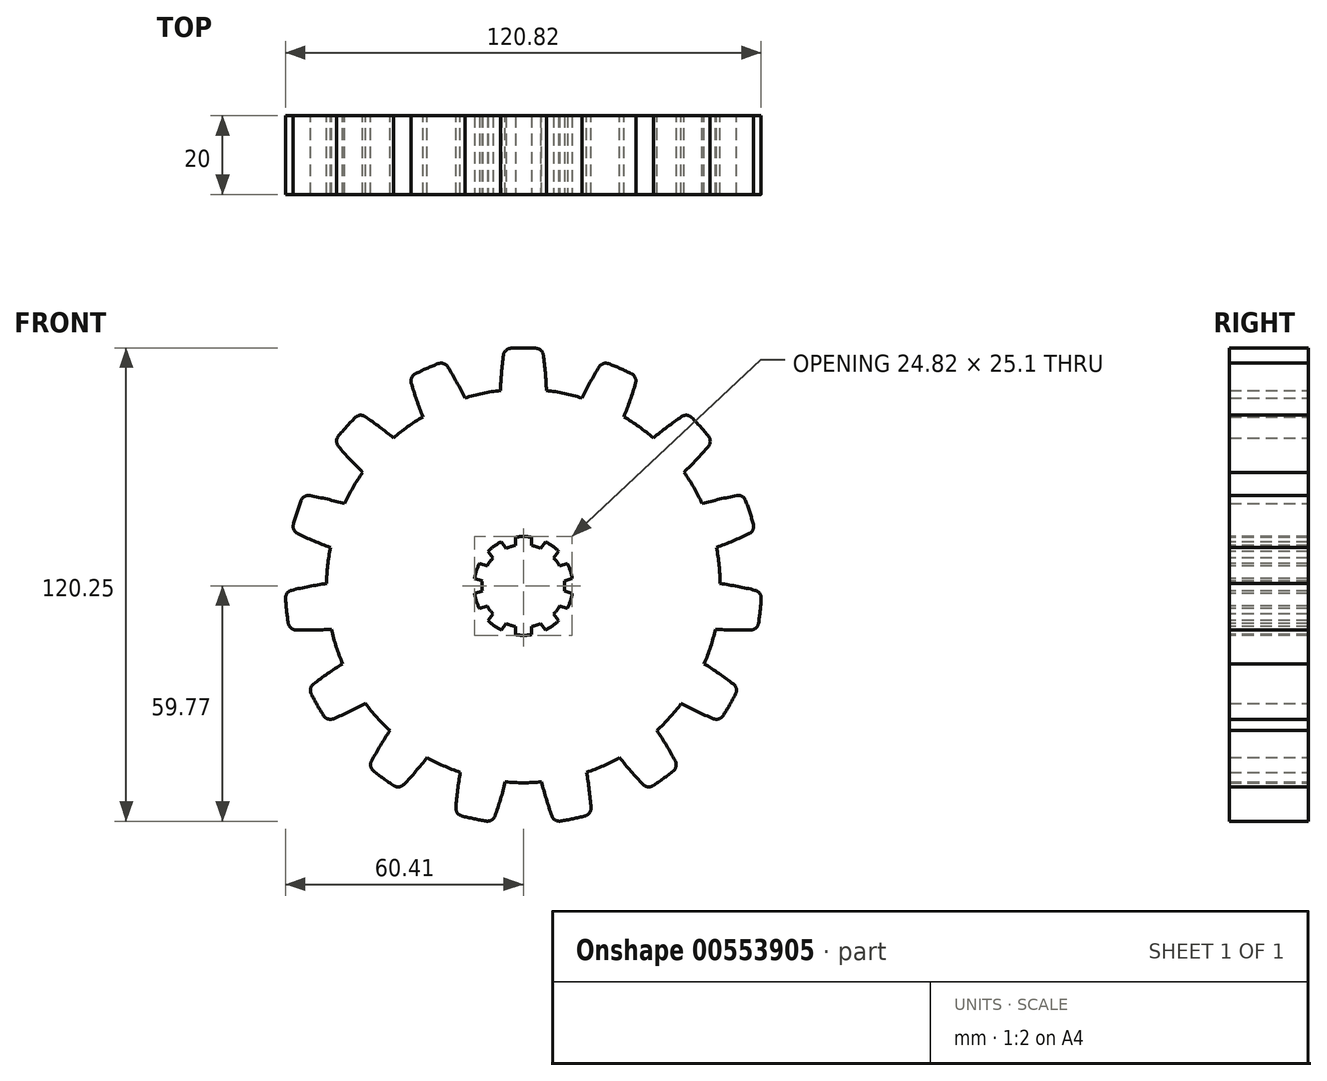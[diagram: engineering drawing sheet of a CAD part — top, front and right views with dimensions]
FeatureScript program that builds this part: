
annotation { "Feature Type Name" : "Feature", "Feature Type Description" : "" }
export const myFeature = defineFeature(function(context is Context, id is Id, definition is map)
    precondition{}
    {
        {
            var Q0;
            Q0=qCreatedBy(makeId("Front.planeOp"),FACE);
            var sketch = newSketch(context, id + "F0", { "sketchPlane" : qUnion([Q0])});
            skCircle(sketch, "E0", {"center": v(0, 0) * mm, "radius": 50 * mm});
            skLineSegment(sketch, "E1", {"start": v(-48.98, 46.5) * mm, "end": v(18.38, 46.5) * mm, "construction": true});
            skLineSegment(sketch, "E2", {"start": v(84.1, 97.1) * mm, "end": v(84.1, -36.75) * mm, "construction": true});
            skArc(sketch, "E3", {"start": v(-4.84, 60.29) * mm, "mid": v(-5.5, 54.99) * mm, "end": v(-5.84, 49.66) * mm});
            skArc(sketch, "E4.MirrorCS", {"start": v(4.84, 60.29) * mm, "mid": v(5.5, 54.99) * mm, "end": v(5.84, 49.66) * mm});
            skArc(sketch, "E5.trimOffspring", {"start": v(4.84, 60.29) * mm, "mid": v(0, 60.48) * mm, "end": v(-4.84, 60.29) * mm});
            skArc(sketch, "E6.1.0", {"start": v(-28.94, 53.11) * mm, "mid": v(-27.39, 48) * mm, "end": v(-25.54, 42.99) * mm});
            skArc(sketch, "E6.1.1", {"start": v(-20.1, 57.05) * mm, "mid": v(-24.6, 55.25) * mm, "end": v(-28.94, 53.11) * mm});
            skArc(sketch, "E6.1.2", {"start": v(-20.1, 57.05) * mm, "mid": v(-17.34, 52.47) * mm, "end": v(-14.86, 47.74) * mm});
            skArc(sketch, "E6.2.0", {"start": v(-48.04, 36.75) * mm, "mid": v(-44.54, 32.7) * mm, "end": v(-40.81, 28.88) * mm});
            skArc(sketch, "E6.2.1", {"start": v(-41.57, 43.94) * mm, "mid": v(-44.95, 40.47) * mm, "end": v(-48.04, 36.75) * mm});
            skArc(sketch, "E6.2.2", {"start": v(-41.57, 43.94) * mm, "mid": v(-37.19, 40.88) * mm, "end": v(-33, 37.57) * mm});
            skArc(sketch, "E6.3.0", {"start": v(-58.83, 14.03) * mm, "mid": v(-54, 11.76) * mm, "end": v(-49.03, 9.79) * mm});
            skArc(sketch, "E6.3.1", {"start": v(-55.84, 23.23) * mm, "mid": v(-57.52, 18.7) * mm, "end": v(-58.83, 14.03) * mm});
            skArc(sketch, "E6.3.2", {"start": v(-55.84, 23.23) * mm, "mid": v(-50.6, 22.22) * mm, "end": v(-45.42, 20.9) * mm});
            skArc(sketch, "E6.4.0", {"start": v(-59.45, -11.11) * mm, "mid": v(-54.11, -11.22) * mm, "end": v(-48.77, -11) * mm});
            skArc(sketch, "E6.4.1", {"start": v(-60.47, -1.5) * mm, "mid": v(-60.15, -6.32) * mm, "end": v(-59.45, -11.11) * mm});
            skArc(sketch, "E6.4.2", {"start": v(-60.47, -1.5) * mm, "mid": v(-55.26, -0.28) * mm, "end": v(-50, 0.62) * mm});
            skArc(sketch, "E6.5.0", {"start": v(-49.8, -34.33) * mm, "mid": v(-44.87, -32.26) * mm, "end": v(-40.08, -29.9) * mm});
            skArc(sketch, "E6.5.1", {"start": v(-54.63, -25.96) * mm, "mid": v(-52.38, -30.24) * mm, "end": v(-49.8, -34.33) * mm});
            skArc(sketch, "E6.5.2", {"start": v(-54.63, -25.96) * mm, "mid": v(-50.37, -22.73) * mm, "end": v(-45.93, -19.77) * mm});
            skArc(sketch, "E6.6.0", {"start": v(-31.52, -51.62) * mm, "mid": v(-27.87, -47.72) * mm, "end": v(-24.46, -43.6) * mm});
            skArc(sketch, "E6.6.1", {"start": v(-39.35, -45.93) * mm, "mid": v(-35.55, -48.93) * mm, "end": v(-31.52, -51.62) * mm});
            skArc(sketch, "E6.6.2", {"start": v(-39.35, -45.93) * mm, "mid": v(-36.77, -41.25) * mm, "end": v(-33.92, -36.74) * mm});
            skArc(sketch, "E6.7.0", {"start": v(-7.8, -59.98) * mm, "mid": v(-6.05, -54.93) * mm, "end": v(-4.6, -49.79) * mm});
            skArc(sketch, "E6.7.1", {"start": v(-17.27, -57.97) * mm, "mid": v(-12.58, -59.16) * mm, "end": v(-7.8, -59.98) * mm});
            skArc(sketch, "E6.7.2", {"start": v(-17.27, -57.97) * mm, "mid": v(-16.81, -52.64) * mm, "end": v(-16.04, -47.36) * mm});
            skArc(sketch, "E6.8.0", {"start": v(17.27, -57.97) * mm, "mid": v(16.81, -52.64) * mm, "end": v(16.04, -47.36) * mm});
            skArc(sketch, "E6.8.1", {"start": v(7.8, -59.98) * mm, "mid": v(12.58, -59.16) * mm, "end": v(17.27, -57.97) * mm});
            skArc(sketch, "E6.8.2", {"start": v(7.8, -59.98) * mm, "mid": v(6.05, -54.93) * mm, "end": v(4.6, -49.79) * mm});
            skArc(sketch, "E6.9.0", {"start": v(39.35, -45.93) * mm, "mid": v(36.77, -41.25) * mm, "end": v(33.92, -36.74) * mm});
            skArc(sketch, "E6.9.1", {"start": v(31.52, -51.62) * mm, "mid": v(35.55, -48.93) * mm, "end": v(39.35, -45.93) * mm});
            skArc(sketch, "E6.9.2", {"start": v(31.52, -51.62) * mm, "mid": v(27.87, -47.72) * mm, "end": v(24.46, -43.6) * mm});
            skArc(sketch, "E6.10.0", {"start": v(54.63, -25.96) * mm, "mid": v(50.37, -22.73) * mm, "end": v(45.93, -19.77) * mm});
            skArc(sketch, "E6.10.1", {"start": v(49.8, -34.33) * mm, "mid": v(52.38, -30.24) * mm, "end": v(54.63, -25.96) * mm});
            skArc(sketch, "E6.10.2", {"start": v(49.8, -34.33) * mm, "mid": v(44.87, -32.26) * mm, "end": v(40.08, -29.9) * mm});
            skArc(sketch, "E6.11.0", {"start": v(60.47, -1.5) * mm, "mid": v(55.26, -0.28) * mm, "end": v(50, 0.62) * mm});
            skArc(sketch, "E6.11.1", {"start": v(59.45, -11.11) * mm, "mid": v(60.15, -6.32) * mm, "end": v(60.47, -1.5) * mm});
            skArc(sketch, "E6.11.2", {"start": v(59.45, -11.11) * mm, "mid": v(54.11, -11.22) * mm, "end": v(48.77, -11) * mm});
            skArc(sketch, "E6.12.0", {"start": v(55.84, 23.23) * mm, "mid": v(50.6, 22.22) * mm, "end": v(45.42, 20.9) * mm});
            skArc(sketch, "E6.12.1", {"start": v(58.83, 14.03) * mm, "mid": v(57.52, 18.7) * mm, "end": v(55.84, 23.23) * mm});
            skArc(sketch, "E6.12.2", {"start": v(58.83, 14.03) * mm, "mid": v(54, 11.76) * mm, "end": v(49.03, 9.79) * mm});
            skArc(sketch, "E6.13.0", {"start": v(41.57, 43.94) * mm, "mid": v(37.19, 40.88) * mm, "end": v(33, 37.57) * mm});
            skArc(sketch, "E6.13.1", {"start": v(48.04, 36.75) * mm, "mid": v(44.95, 40.47) * mm, "end": v(41.57, 43.94) * mm});
            skArc(sketch, "E6.13.2", {"start": v(48.04, 36.75) * mm, "mid": v(44.54, 32.7) * mm, "end": v(40.81, 28.88) * mm});
            skArc(sketch, "E6.14.0", {"start": v(20.1, 57.05) * mm, "mid": v(17.34, 52.47) * mm, "end": v(14.86, 47.74) * mm});
            skArc(sketch, "E6.14.1", {"start": v(28.94, 53.11) * mm, "mid": v(24.6, 55.25) * mm, "end": v(20.1, 57.05) * mm});
            skArc(sketch, "E6.14.2", {"start": v(28.94, 53.11) * mm, "mid": v(27.39, 48) * mm, "end": v(25.54, 42.99) * mm});
            skSolve(sketch);
        }
        {
            var Q0;
            {var subQ0=sQuery(id+"F0.wireOp",EDGE,"E0");var subQ18=makeQuery(id+"F0.imprint","INTERSECT",VERTEX,{"derivedFrom":[subQ0,sQuery(id+"F0.wireOp",EDGE,"E6.11.0")]});Q0=makeQuery(id+"F0.imprint","IMPRINT",FACE,{"disambiguationData":[TD([[makeQuery(id+"F0.imprint","IMPRINT",EDGE,{"disambiguationData":[TD([[subQ18,-1.0]])],"derivedFrom":subQ0}),1.0]])]});}
            var Q1;
            {var subQ0=sQuery(id+"F0.wireOp",EDGE,"E6.1.0");Q1=makeQuery(id+"F0.imprint","IMPRINT",FACE,{"disambiguationData":[TD([[makeQuery(id+"F0.imprint","IMPRINT",EDGE,{"derivedFrom":subQ0}),1.0]])]});}
            var Q2;
            {var subQ0=sQuery(id+"F0.wireOp",EDGE,"E3");Q2=makeQuery(id+"F0.imprint","IMPRINT",FACE,{"disambiguationData":[TD([[makeQuery(id+"F0.imprint","IMPRINT",EDGE,{"derivedFrom":subQ0}),1.0]])]});}
            var Q3;
            {var subQ0=sQuery(id+"F0.wireOp",EDGE,"E6.14.0");Q3=makeQuery(id+"F0.imprint","IMPRINT",FACE,{"disambiguationData":[TD([[makeQuery(id+"F0.imprint","IMPRINT",EDGE,{"derivedFrom":subQ0}),1.0]])]});}
            var Q4;
            {var subQ0=sQuery(id+"F0.wireOp",EDGE,"E6.13.0");Q4=makeQuery(id+"F0.imprint","IMPRINT",FACE,{"disambiguationData":[TD([[makeQuery(id+"F0.imprint","IMPRINT",EDGE,{"derivedFrom":subQ0}),1.0]])]});}
            var Q5;
            {var subQ0=sQuery(id+"F0.wireOp",EDGE,"E6.12.0");Q5=makeQuery(id+"F0.imprint","IMPRINT",FACE,{"disambiguationData":[TD([[makeQuery(id+"F0.imprint","IMPRINT",EDGE,{"derivedFrom":subQ0}),1.0]])]});}
            var Q6;
            {var subQ0=sQuery(id+"F0.wireOp",EDGE,"E6.11.0");Q6=makeQuery(id+"F0.imprint","IMPRINT",FACE,{"disambiguationData":[TD([[makeQuery(id+"F0.imprint","IMPRINT",EDGE,{"derivedFrom":subQ0}),1.0]])]});}
            var Q7;
            {var subQ0=sQuery(id+"F0.wireOp",EDGE,"E6.10.0");Q7=makeQuery(id+"F0.imprint","IMPRINT",FACE,{"disambiguationData":[TD([[makeQuery(id+"F0.imprint","IMPRINT",EDGE,{"derivedFrom":subQ0}),1.0]])]});}
            var Q8;
            {var subQ0=sQuery(id+"F0.wireOp",EDGE,"E6.9.0");Q8=makeQuery(id+"F0.imprint","IMPRINT",FACE,{"disambiguationData":[TD([[makeQuery(id+"F0.imprint","IMPRINT",EDGE,{"derivedFrom":subQ0}),1.0]])]});}
            var Q9;
            {var subQ0=sQuery(id+"F0.wireOp",EDGE,"E6.8.0");Q9=makeQuery(id+"F0.imprint","IMPRINT",FACE,{"disambiguationData":[TD([[makeQuery(id+"F0.imprint","IMPRINT",EDGE,{"derivedFrom":subQ0}),1.0]])]});}
            var Q10;
            {var subQ0=sQuery(id+"F0.wireOp",EDGE,"E6.7.0");Q10=makeQuery(id+"F0.imprint","IMPRINT",FACE,{"disambiguationData":[TD([[makeQuery(id+"F0.imprint","IMPRINT",EDGE,{"derivedFrom":subQ0}),1.0]])]});}
            var Q11;
            {var subQ0=sQuery(id+"F0.wireOp",EDGE,"E6.6.0");Q11=makeQuery(id+"F0.imprint","IMPRINT",FACE,{"disambiguationData":[TD([[makeQuery(id+"F0.imprint","IMPRINT",EDGE,{"derivedFrom":subQ0}),1.0]])]});}
            var Q12;
            {var subQ0=sQuery(id+"F0.wireOp",EDGE,"E6.5.0");Q12=makeQuery(id+"F0.imprint","IMPRINT",FACE,{"disambiguationData":[TD([[makeQuery(id+"F0.imprint","IMPRINT",EDGE,{"derivedFrom":subQ0}),1.0]])]});}
            var Q13;
            {var subQ0=sQuery(id+"F0.wireOp",EDGE,"E6.4.0");Q13=makeQuery(id+"F0.imprint","IMPRINT",FACE,{"disambiguationData":[TD([[makeQuery(id+"F0.imprint","IMPRINT",EDGE,{"derivedFrom":subQ0}),1.0]])]});}
            var Q14;
            {var subQ0=sQuery(id+"F0.wireOp",EDGE,"E6.3.0");Q14=makeQuery(id+"F0.imprint","IMPRINT",FACE,{"disambiguationData":[TD([[makeQuery(id+"F0.imprint","IMPRINT",EDGE,{"derivedFrom":subQ0}),1.0]])]});}
            var Q15;
            {var subQ0=sQuery(id+"F0.wireOp",EDGE,"E6.2.0");Q15=makeQuery(id+"F0.imprint","IMPRINT",FACE,{"disambiguationData":[TD([[makeQuery(id+"F0.imprint","IMPRINT",EDGE,{"derivedFrom":subQ0}),1.0]])]});}
            extrude(context, id + "F1", {"entities" : qUnion([Q0, Q1, Q2, Q3, Q4, Q5, Q6, Q7, Q8, Q9, Q10, Q11, Q12, Q13, Q14, Q15]), "depth" : 20 * mm, "offsetDistance" : 25 * mm});
        }
        {
            var Q0;
            Q0=makeQuery(id+"F1.opExtrude","CAP_FACE",FACE,{"disambiguationData":[OSD([sQuery(id+"F0.wireOp",EDGE,"E0"),sQuery(id+"F0.wireOp",EDGE,"E3"),sQuery(id+"F0.wireOp",EDGE,"E4.MirrorCS"),sQuery(id+"F0.wireOp",EDGE,"E5.trimOffspring"),sQuery(id+"F0.wireOp",EDGE,"E6.1.0"),sQuery(id+"F0.wireOp",EDGE,"E6.1.1"),sQuery(id+"F0.wireOp",EDGE,"E6.1.2"),sQuery(id+"F0.wireOp",EDGE,"E6.2.0"),sQuery(id+"F0.wireOp",EDGE,"E6.2.1"),sQuery(id+"F0.wireOp",EDGE,"E6.2.2"),sQuery(id+"F0.wireOp",EDGE,"E6.3.0"),sQuery(id+"F0.wireOp",EDGE,"E6.3.1"),sQuery(id+"F0.wireOp",EDGE,"E6.3.2"),sQuery(id+"F0.wireOp",EDGE,"E6.4.0"),sQuery(id+"F0.wireOp",EDGE,"E6.4.1"),sQuery(id+"F0.wireOp",EDGE,"E6.4.2"),sQuery(id+"F0.wireOp",EDGE,"E6.5.0"),sQuery(id+"F0.wireOp",EDGE,"E6.5.1"),sQuery(id+"F0.wireOp",EDGE,"E6.5.2"),sQuery(id+"F0.wireOp",EDGE,"E6.6.0"),sQuery(id+"F0.wireOp",EDGE,"E6.6.1"),sQuery(id+"F0.wireOp",EDGE,"E6.6.2"),sQuery(id+"F0.wireOp",EDGE,"E6.7.0"),sQuery(id+"F0.wireOp",EDGE,"E6.7.1"),sQuery(id+"F0.wireOp",EDGE,"E6.7.2"),sQuery(id+"F0.wireOp",EDGE,"E6.8.0"),sQuery(id+"F0.wireOp",EDGE,"E6.8.1"),sQuery(id+"F0.wireOp",EDGE,"E6.8.2"),sQuery(id+"F0.wireOp",EDGE,"E6.9.0"),sQuery(id+"F0.wireOp",EDGE,"E6.9.1"),sQuery(id+"F0.wireOp",EDGE,"E6.9.2"),sQuery(id+"F0.wireOp",EDGE,"E6.10.0"),sQuery(id+"F0.wireOp",EDGE,"E6.10.1"),sQuery(id+"F0.wireOp",EDGE,"E6.10.2"),sQuery(id+"F0.wireOp",EDGE,"E6.11.0"),sQuery(id+"F0.wireOp",EDGE,"E6.11.1"),sQuery(id+"F0.wireOp",EDGE,"E6.11.2"),sQuery(id+"F0.wireOp",EDGE,"E6.12.0"),sQuery(id+"F0.wireOp",EDGE,"E6.12.1"),sQuery(id+"F0.wireOp",EDGE,"E6.12.2"),sQuery(id+"F0.wireOp",EDGE,"E6.13.0"),sQuery(id+"F0.wireOp",EDGE,"E6.13.1"),sQuery(id+"F0.wireOp",EDGE,"E6.13.2"),sQuery(id+"F0.wireOp",EDGE,"E6.14.0"),sQuery(id+"F0.wireOp",EDGE,"E6.14.1"),sQuery(id+"F0.wireOp",EDGE,"E6.14.2")])],"isStart":false});
            var sketch = newSketch(context, id + "F2", { "sketchPlane" : qUnion([Q0])});
            skCircle(sketch, "E7", {"center": v(0, 0) * mm, "radius": 10.5 * mm});
            skArc(sketch, "E8", {"start": v(2.05, 12.38) * mm, "mid": v(0, 12.55) * mm, "end": v(-2.05, 12.38) * mm});
            skLineSegment(sketch, "E9", {"start": v(-2.05, 12.38) * mm, "end": v(-2.05, 10.3) * mm});
            skLineSegment(sketch, "E10", {"start": v(2.05, 12.38) * mm, "end": v(2.05, 10.3) * mm});
            skLineSegment(sketch, "E11.1.0", {"start": v(-8.94, 8.81) * mm, "end": v(-7.71, 7.13) * mm});
            skArc(sketch, "E11.1.1", {"start": v(-5.62, 11.22) * mm, "mid": v(-7.38, 10.15) * mm, "end": v(-8.94, 8.81) * mm});
            skLineSegment(sketch, "E11.1.2", {"start": v(-5.62, 11.22) * mm, "end": v(-4.4, 9.54) * mm});
            skLineSegment(sketch, "E11.2.0", {"start": v(-12.4, 1.88) * mm, "end": v(-10.43, 1.23) * mm});
            skArc(sketch, "E11.2.1", {"start": v(-11.14, 5.78) * mm, "mid": v(-11.94, 3.88) * mm, "end": v(-12.4, 1.88) * mm});
            skLineSegment(sketch, "E11.2.2", {"start": v(-11.14, 5.78) * mm, "end": v(-9.16, 5.13) * mm});
            skLineSegment(sketch, "E11.3.0", {"start": v(-11.14, -5.78) * mm, "end": v(-9.16, -5.13) * mm});
            skArc(sketch, "E11.3.1", {"start": v(-12.4, -1.88) * mm, "mid": v(-11.94, -3.88) * mm, "end": v(-11.14, -5.78) * mm});
            skLineSegment(sketch, "E11.3.2", {"start": v(-12.4, -1.88) * mm, "end": v(-10.43, -1.23) * mm});
            skLineSegment(sketch, "E11.4.0", {"start": v(-5.62, -11.22) * mm, "end": v(-4.4, -9.54) * mm});
            skArc(sketch, "E11.4.1", {"start": v(-8.94, -8.81) * mm, "mid": v(-7.38, -10.15) * mm, "end": v(-5.62, -11.22) * mm});
            skLineSegment(sketch, "E11.4.2", {"start": v(-8.94, -8.81) * mm, "end": v(-7.71, -7.13) * mm});
            skLineSegment(sketch, "E11.5.0", {"start": v(2.05, -12.38) * mm, "end": v(2.05, -10.3) * mm});
            skArc(sketch, "E11.5.1", {"start": v(-2.05, -12.38) * mm, "mid": v(0, -12.55) * mm, "end": v(2.05, -12.38) * mm});
            skLineSegment(sketch, "E11.5.2", {"start": v(-2.05, -12.38) * mm, "end": v(-2.05, -10.3) * mm});
            skLineSegment(sketch, "E11.6.0", {"start": v(8.94, -8.81) * mm, "end": v(7.71, -7.13) * mm});
            skArc(sketch, "E11.6.1", {"start": v(5.62, -11.22) * mm, "mid": v(7.38, -10.15) * mm, "end": v(8.94, -8.81) * mm});
            skLineSegment(sketch, "E11.6.2", {"start": v(5.62, -11.22) * mm, "end": v(4.4, -9.54) * mm});
            skLineSegment(sketch, "E11.7.0", {"start": v(12.4, -1.88) * mm, "end": v(10.43, -1.23) * mm});
            skArc(sketch, "E11.7.1", {"start": v(11.14, -5.78) * mm, "mid": v(11.94, -3.88) * mm, "end": v(12.4, -1.88) * mm});
            skLineSegment(sketch, "E11.7.2", {"start": v(11.14, -5.78) * mm, "end": v(9.16, -5.13) * mm});
            skLineSegment(sketch, "E11.8.0", {"start": v(11.14, 5.78) * mm, "end": v(9.16, 5.13) * mm});
            skArc(sketch, "E11.8.1", {"start": v(12.4, 1.88) * mm, "mid": v(11.94, 3.88) * mm, "end": v(11.14, 5.78) * mm});
            skLineSegment(sketch, "E11.8.2", {"start": v(12.4, 1.88) * mm, "end": v(10.43, 1.23) * mm});
            skLineSegment(sketch, "E11.9.0", {"start": v(5.62, 11.22) * mm, "end": v(4.4, 9.54) * mm});
            skArc(sketch, "E11.9.1", {"start": v(8.94, 8.81) * mm, "mid": v(7.38, 10.15) * mm, "end": v(5.62, 11.22) * mm});
            skLineSegment(sketch, "E11.9.2", {"start": v(8.94, 8.81) * mm, "end": v(7.71, 7.13) * mm});
            skSolve(sketch);
        }
        {
            var Q0;
            {var subQ0=sQuery(id+"F2.wireOp",EDGE,"E7");var subQ8=makeQuery(id+"F2.imprint","INTERSECT",VERTEX,{"derivedFrom":[subQ0,sQuery(id+"F2.wireOp",EDGE,"E11.8.0")]});Q0=makeQuery(id+"F2.imprint","IMPRINT",FACE,{"disambiguationData":[TD([[makeQuery(id+"F2.imprint","IMPRINT",EDGE,{"disambiguationData":[TD([[subQ8,1.0]])],"derivedFrom":subQ0}),1.0]])]});}
            var Q1;
            {var subQ0=sQuery(id+"F2.wireOp",EDGE,"E11.1.0");Q1=makeQuery(id+"F2.imprint","IMPRINT",FACE,{"disambiguationData":[TD([[makeQuery(id+"F2.imprint","IMPRINT",EDGE,{"derivedFrom":subQ0}),1.0]])]});}
            var Q2;
            Q2=makeQuery(id+"F2.imprint","IMPRINT",FACE,{"disambiguationData":[TD([[makeQuery(id+"F2.imprint","IMPRINT",EDGE,{"derivedFrom":sQuery(id+"F2.wireOp",EDGE,"E8")}),1.0]])]});
            var Q3;
            {var subQ0=sQuery(id+"F2.wireOp",EDGE,"E11.9.0");Q3=makeQuery(id+"F2.imprint","IMPRINT",FACE,{"disambiguationData":[TD([[makeQuery(id+"F2.imprint","IMPRINT",EDGE,{"derivedFrom":subQ0}),1.0]])]});}
            var Q4;
            {var subQ0=sQuery(id+"F2.wireOp",EDGE,"E11.2.0");Q4=makeQuery(id+"F2.imprint","IMPRINT",FACE,{"disambiguationData":[TD([[makeQuery(id+"F2.imprint","IMPRINT",EDGE,{"derivedFrom":subQ0}),1.0]])]});}
            var Q5;
            {var subQ0=sQuery(id+"F2.wireOp",EDGE,"E11.3.0");Q5=makeQuery(id+"F2.imprint","IMPRINT",FACE,{"disambiguationData":[TD([[makeQuery(id+"F2.imprint","IMPRINT",EDGE,{"derivedFrom":subQ0}),1.0]])]});}
            var Q6;
            {var subQ0=sQuery(id+"F2.wireOp",EDGE,"E11.4.0");Q6=makeQuery(id+"F2.imprint","IMPRINT",FACE,{"disambiguationData":[TD([[makeQuery(id+"F2.imprint","IMPRINT",EDGE,{"derivedFrom":subQ0}),1.0]])]});}
            var Q7;
            {var subQ0=sQuery(id+"F2.wireOp",EDGE,"E11.5.0");Q7=makeQuery(id+"F2.imprint","IMPRINT",FACE,{"disambiguationData":[TD([[makeQuery(id+"F2.imprint","IMPRINT",EDGE,{"derivedFrom":subQ0}),1.0]])]});}
            var Q8;
            {var subQ0=sQuery(id+"F2.wireOp",EDGE,"E11.6.0");Q8=makeQuery(id+"F2.imprint","IMPRINT",FACE,{"disambiguationData":[TD([[makeQuery(id+"F2.imprint","IMPRINT",EDGE,{"derivedFrom":subQ0}),1.0]])]});}
            var Q9;
            {var subQ0=sQuery(id+"F2.wireOp",EDGE,"E11.7.0");Q9=makeQuery(id+"F2.imprint","IMPRINT",FACE,{"disambiguationData":[TD([[makeQuery(id+"F2.imprint","IMPRINT",EDGE,{"derivedFrom":subQ0}),1.0]])]});}
            var Q10;
            {var subQ0=sQuery(id+"F2.wireOp",EDGE,"E11.8.0");Q10=makeQuery(id+"F2.imprint","IMPRINT",FACE,{"disambiguationData":[TD([[makeQuery(id+"F2.imprint","IMPRINT",EDGE,{"derivedFrom":subQ0}),1.0]])]});}
            extrude(context, id + "F3", {"entities" : qUnion([Q0, Q1, Q2, Q3, Q4, Q5, Q6, Q7, Q8, Q9, Q10]), "operationType" : NewBodyOperationType.REMOVE, "oppositeDirection" : true, "depth" : 20 * mm, "offsetDistance" : 25 * mm});
        }
        {
            var Q0;
            Q0=makeQuery(id+"F1.opExtrude","SWEPT_EDGE",EDGE,{"disambiguationData":[OSD([sQuery(id+"F0.wireOp",EDGE,"E6.1.1"),sQuery(id+"F0.wireOp",EDGE,"E6.1.2")])]});
            var Q1;
            Q1=makeQuery(id+"F1.opExtrude","SWEPT_EDGE",EDGE,{"disambiguationData":[OSD([sQuery(id+"F0.wireOp",EDGE,"E3"),sQuery(id+"F0.wireOp",EDGE,"E5.trimOffspring")])]});
            var Q2;
            Q2=makeQuery(id+"F1.opExtrude","SWEPT_EDGE",EDGE,{"disambiguationData":[OSD([sQuery(id+"F0.wireOp",EDGE,"E6.14.0"),sQuery(id+"F0.wireOp",EDGE,"E6.14.1")])]});
            var Q3;
            Q3=makeQuery(id+"F1.opExtrude","SWEPT_EDGE",EDGE,{"disambiguationData":[OSD([sQuery(id+"F0.wireOp",EDGE,"E4.MirrorCS"),sQuery(id+"F0.wireOp",EDGE,"E5.trimOffspring")])]});
            var Q4;
            Q4=makeQuery(id+"F1.opExtrude","SWEPT_EDGE",EDGE,{"disambiguationData":[OSD([sQuery(id+"F0.wireOp",EDGE,"E6.14.1"),sQuery(id+"F0.wireOp",EDGE,"E6.14.2")])]});
            var Q5;
            Q5=makeQuery(id+"F1.opExtrude","SWEPT_EDGE",EDGE,{"disambiguationData":[OSD([sQuery(id+"F0.wireOp",EDGE,"E6.13.0"),sQuery(id+"F0.wireOp",EDGE,"E6.13.1")])]});
            var Q6;
            Q6=makeQuery(id+"F1.opExtrude","SWEPT_EDGE",EDGE,{"disambiguationData":[OSD([sQuery(id+"F0.wireOp",EDGE,"E6.13.1"),sQuery(id+"F0.wireOp",EDGE,"E6.13.2")])]});
            var Q7;
            Q7=makeQuery(id+"F1.opExtrude","SWEPT_EDGE",EDGE,{"disambiguationData":[OSD([sQuery(id+"F0.wireOp",EDGE,"E6.12.0"),sQuery(id+"F0.wireOp",EDGE,"E6.12.1")])]});
            var Q8;
            Q8=makeQuery(id+"F1.opExtrude","SWEPT_EDGE",EDGE,{"disambiguationData":[OSD([sQuery(id+"F0.wireOp",EDGE,"E6.11.0"),sQuery(id+"F0.wireOp",EDGE,"E6.11.1")])]});
            var Q9;
            Q9=makeQuery(id+"F1.opExtrude","SWEPT_EDGE",EDGE,{"disambiguationData":[OSD([sQuery(id+"F0.wireOp",EDGE,"E6.11.1"),sQuery(id+"F0.wireOp",EDGE,"E6.11.2")])]});
            var Q10;
            Q10=makeQuery(id+"F1.opExtrude","SWEPT_EDGE",EDGE,{"disambiguationData":[OSD([sQuery(id+"F0.wireOp",EDGE,"E6.10.0"),sQuery(id+"F0.wireOp",EDGE,"E6.10.1")])]});
            var Q11;
            Q11=makeQuery(id+"F1.opExtrude","SWEPT_EDGE",EDGE,{"disambiguationData":[OSD([sQuery(id+"F0.wireOp",EDGE,"E6.10.1"),sQuery(id+"F0.wireOp",EDGE,"E6.10.2")])]});
            var Q12;
            Q12=makeQuery(id+"F1.opExtrude","SWEPT_EDGE",EDGE,{"disambiguationData":[OSD([sQuery(id+"F0.wireOp",EDGE,"E6.9.0"),sQuery(id+"F0.wireOp",EDGE,"E6.9.1")])]});
            var Q13;
            Q13=makeQuery(id+"F1.opExtrude","SWEPT_EDGE",EDGE,{"disambiguationData":[OSD([sQuery(id+"F0.wireOp",EDGE,"E6.9.1"),sQuery(id+"F0.wireOp",EDGE,"E6.9.2")])]});
            var Q14;
            Q14=makeQuery(id+"F1.opExtrude","SWEPT_EDGE",EDGE,{"disambiguationData":[OSD([sQuery(id+"F0.wireOp",EDGE,"E6.8.0"),sQuery(id+"F0.wireOp",EDGE,"E6.8.1")])]});
            var Q15;
            Q15=makeQuery(id+"F1.opExtrude","SWEPT_EDGE",EDGE,{"disambiguationData":[OSD([sQuery(id+"F0.wireOp",EDGE,"E6.6.0"),sQuery(id+"F0.wireOp",EDGE,"E6.6.1")])]});
            var Q16;
            Q16=makeQuery(id+"F1.opExtrude","SWEPT_EDGE",EDGE,{"disambiguationData":[OSD([sQuery(id+"F0.wireOp",EDGE,"E6.7.1"),sQuery(id+"F0.wireOp",EDGE,"E6.7.2")])]});
            var Q17;
            Q17=makeQuery(id+"F1.opExtrude","SWEPT_EDGE",EDGE,{"disambiguationData":[OSD([sQuery(id+"F0.wireOp",EDGE,"E6.8.1"),sQuery(id+"F0.wireOp",EDGE,"E6.8.2")])]});
            var Q18;
            Q18=makeQuery(id+"F1.opExtrude","SWEPT_EDGE",EDGE,{"disambiguationData":[OSD([sQuery(id+"F0.wireOp",EDGE,"E6.7.0"),sQuery(id+"F0.wireOp",EDGE,"E6.7.1")])]});
            var Q19;
            Q19=makeQuery(id+"F1.opExtrude","SWEPT_EDGE",EDGE,{"disambiguationData":[OSD([sQuery(id+"F0.wireOp",EDGE,"E6.12.1"),sQuery(id+"F0.wireOp",EDGE,"E6.12.2")])]});
            var Q20;
            Q20=makeQuery(id+"F1.opExtrude","SWEPT_EDGE",EDGE,{"disambiguationData":[OSD([sQuery(id+"F0.wireOp",EDGE,"E6.6.1"),sQuery(id+"F0.wireOp",EDGE,"E6.6.2")])]});
            var Q21;
            Q21=makeQuery(id+"F1.opExtrude","SWEPT_EDGE",EDGE,{"disambiguationData":[OSD([sQuery(id+"F0.wireOp",EDGE,"E6.5.0"),sQuery(id+"F0.wireOp",EDGE,"E6.5.1")])]});
            var Q22;
            Q22=makeQuery(id+"F1.opExtrude","SWEPT_EDGE",EDGE,{"disambiguationData":[OSD([sQuery(id+"F0.wireOp",EDGE,"E6.5.1"),sQuery(id+"F0.wireOp",EDGE,"E6.5.2")])]});
            var Q23;
            Q23=makeQuery(id+"F1.opExtrude","SWEPT_EDGE",EDGE,{"disambiguationData":[OSD([sQuery(id+"F0.wireOp",EDGE,"E6.4.0"),sQuery(id+"F0.wireOp",EDGE,"E6.4.1")])]});
            var Q24;
            Q24=makeQuery(id+"F1.opExtrude","SWEPT_EDGE",EDGE,{"disambiguationData":[OSD([sQuery(id+"F0.wireOp",EDGE,"E6.3.0"),sQuery(id+"F0.wireOp",EDGE,"E6.3.1")])]});
            var Q25;
            Q25=makeQuery(id+"F1.opExtrude","SWEPT_EDGE",EDGE,{"disambiguationData":[OSD([sQuery(id+"F0.wireOp",EDGE,"E6.3.1"),sQuery(id+"F0.wireOp",EDGE,"E6.3.2")])]});
            var Q26;
            Q26=makeQuery(id+"F1.opExtrude","SWEPT_EDGE",EDGE,{"disambiguationData":[OSD([sQuery(id+"F0.wireOp",EDGE,"E6.4.1"),sQuery(id+"F0.wireOp",EDGE,"E6.4.2")])]});
            var Q27;
            Q27=makeQuery(id+"F1.opExtrude","SWEPT_EDGE",EDGE,{"disambiguationData":[OSD([sQuery(id+"F0.wireOp",EDGE,"E6.2.0"),sQuery(id+"F0.wireOp",EDGE,"E6.2.1")])]});
            var Q28;
            Q28=makeQuery(id+"F1.opExtrude","SWEPT_EDGE",EDGE,{"disambiguationData":[OSD([sQuery(id+"F0.wireOp",EDGE,"E6.1.0"),sQuery(id+"F0.wireOp",EDGE,"E6.1.1")])]});
            var Q29;
            Q29=makeQuery(id+"F1.opExtrude","SWEPT_EDGE",EDGE,{"disambiguationData":[OSD([sQuery(id+"F0.wireOp",EDGE,"E6.2.1"),sQuery(id+"F0.wireOp",EDGE,"E6.2.2")])]});
            fillet(context, id + "F4", {"entities" : qUnion([Q0, Q1, Q2, Q3, Q4, Q5, Q6, Q7, Q8, Q9, Q10, Q11, Q12, Q13, Q14, Q15, Q16, Q17, Q18, Q19, Q20, Q21, Q22, Q23, Q24, Q25, Q26, Q27, Q28, Q29]), "radius" : 2 * mm, "tangentPropagation" : true, "allowEdgeOverflow" : false});
        }
    });
